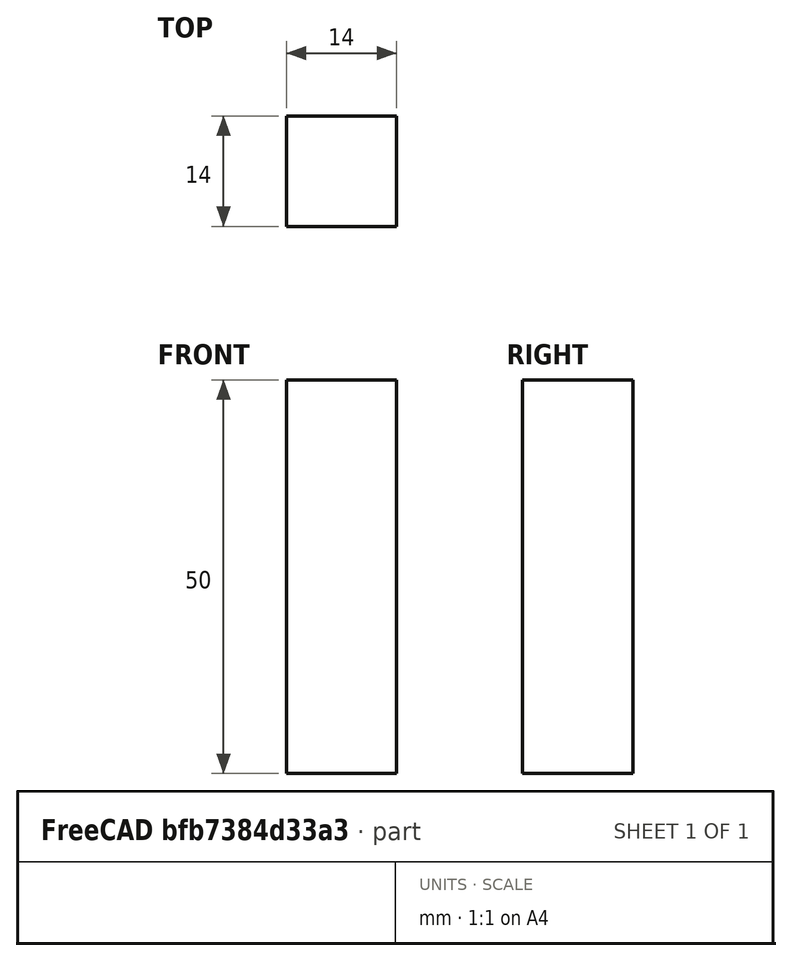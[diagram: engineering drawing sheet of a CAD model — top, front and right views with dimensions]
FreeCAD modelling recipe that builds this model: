
FCSTD DOCUMENT  (FreeCAD 0.15R4671 (Git))
Label: Square Bar 14 EN10059 S235JR
License: All rights reserved
LicenseURL: http://en.wikipedia.org/wiki/All_rights_reserved
objects: Sketcher::SketchObject×1, Part::Extrusion×1
note: 2 computed .brp shape members not serialized (recipe doc carries the construction recipe); baked Part::Feature solids carry a one-line shape summary decoded from their .brp

FEATURE [Sketcher::SketchObject] Sketch
  sketch-geometry (4):
    g0: LineSegment StartX=-7 StartY=-7 StartZ=0 EndX=7 EndY=-7 EndZ=0
    g1: LineSegment StartX=7 StartY=-7 StartZ=0 EndX=7 EndY=7 EndZ=0
    g2: LineSegment StartX=7 StartY=7 StartZ=0 EndX=-7 EndY=7 EndZ=0
    g3: LineSegment StartX=-7 StartY=7 StartZ=0 EndX=-7 EndY=-7 EndZ=0
  constraints (12):
    c: Coincident(g0,g1)
    c: Coincident(g1,g2)
    c: Coincident(g2,g3)
    c: Coincident(g3,g0)
    c: Horizontal(g0)
    c: Horizontal(g2)
    c: Vertical(g1)
    c: Vertical(g3)
    c: Symmetric(g1,g0,g-1)
    c: Symmetric(g2,g1,g-2)
    c: Equal(g1,g2)
    c: DistanceY(g1) = 14
FEATURE [Part::Extrusion] Extrude  label="Square Bar 14 EN10059 S235JR"
  Base = -> Sketch
  Dir = (0,0,50)
  Solid = true
